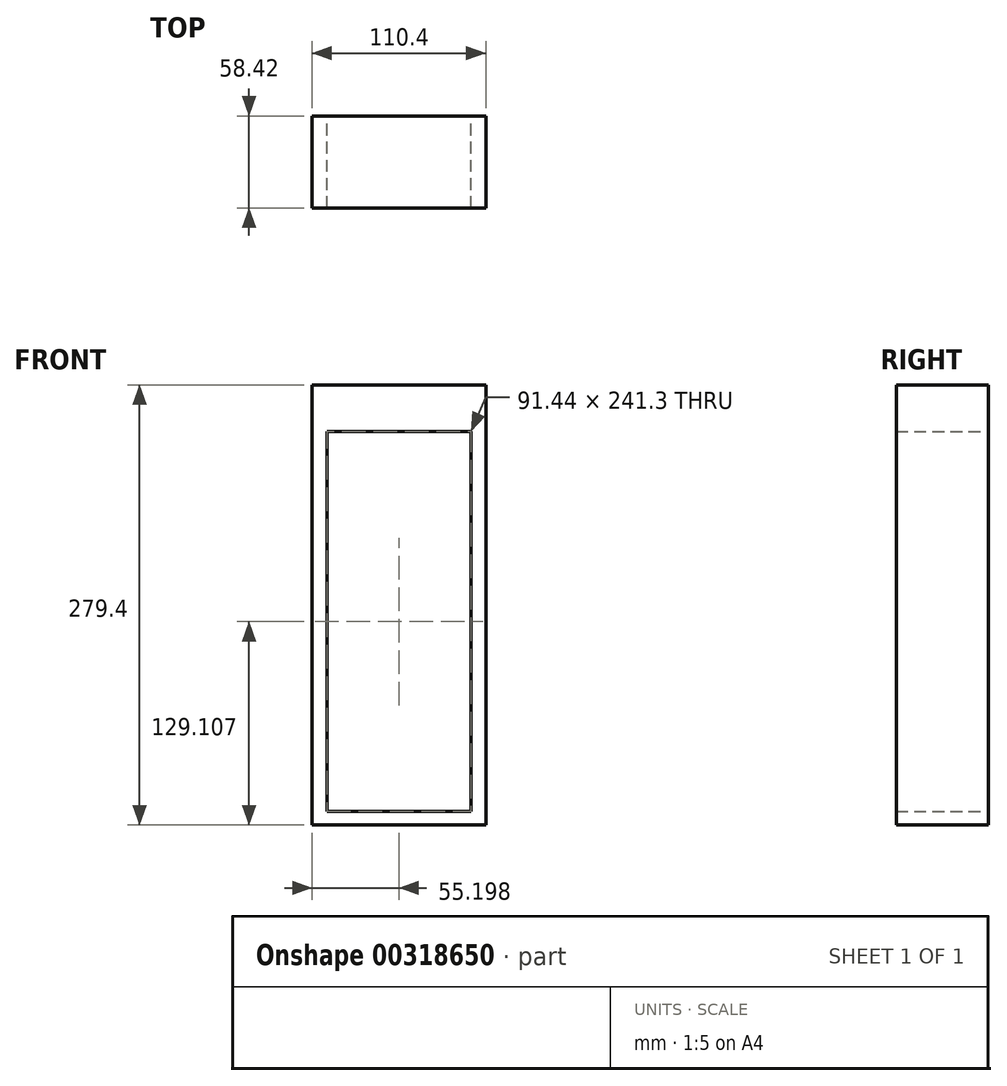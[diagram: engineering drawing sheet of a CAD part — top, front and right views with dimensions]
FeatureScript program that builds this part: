
annotation { "Feature Type Name" : "Feature", "Feature Type Description" : "" }
export const myFeature = defineFeature(function(context is Context, id is Id, definition is map)
    precondition{}
    {
        {
            var Q0;
            Q0=qCreatedBy(makeId("Front.planeOp"),FACE);
            var sketch = newSketch(context, id + "F0", { "sketchPlane" : qUnion([Q0])});
            skLineSegment(sketch, "E0.bottom", {"start": v(-72.2, -140.3) * mm, "end": v(38.2, -140.3) * mm});
            skLineSegment(sketch, "E0.top", {"start": v(-72.2, 139.1) * mm, "end": v(38.2, 139.1) * mm});
            skLineSegment(sketch, "E0.left", {"start": v(-72.2, -140.3) * mm, "end": v(-72.2, 139.1) * mm});
            skLineSegment(sketch, "E0.right", {"start": v(38.2, -140.3) * mm, "end": v(38.2, 139.1) * mm});
            skLineSegment(sketch, "E1.bottom", {"start": v(-62.72, -131.84) * mm, "end": v(28.72, -131.84) * mm});
            skLineSegment(sketch, "E1.top", {"start": v(-62.72, 109.46) * mm, "end": v(28.72, 109.46) * mm});
            skLineSegment(sketch, "E1.left", {"start": v(-62.72, -131.84) * mm, "end": v(-62.72, 109.46) * mm});
            skLineSegment(sketch, "E1.right", {"start": v(28.72, -131.84) * mm, "end": v(28.72, 109.46) * mm});
            skLineSegment(sketch, "E2", {"start": v(28.72, 109.46) * mm, "end": v(38.2, 109.46) * mm});
            skSolve(sketch);
        }
        {
            var Q0;
            Q0 = qSketchRegion(id + "F0", true);
            extrude(context, id + "F1", {"entities" : qUnion([Q0]), "endBound" : BoundingType.SYMMETRIC, "depth" : 58.42 * mm});
        }
    });
